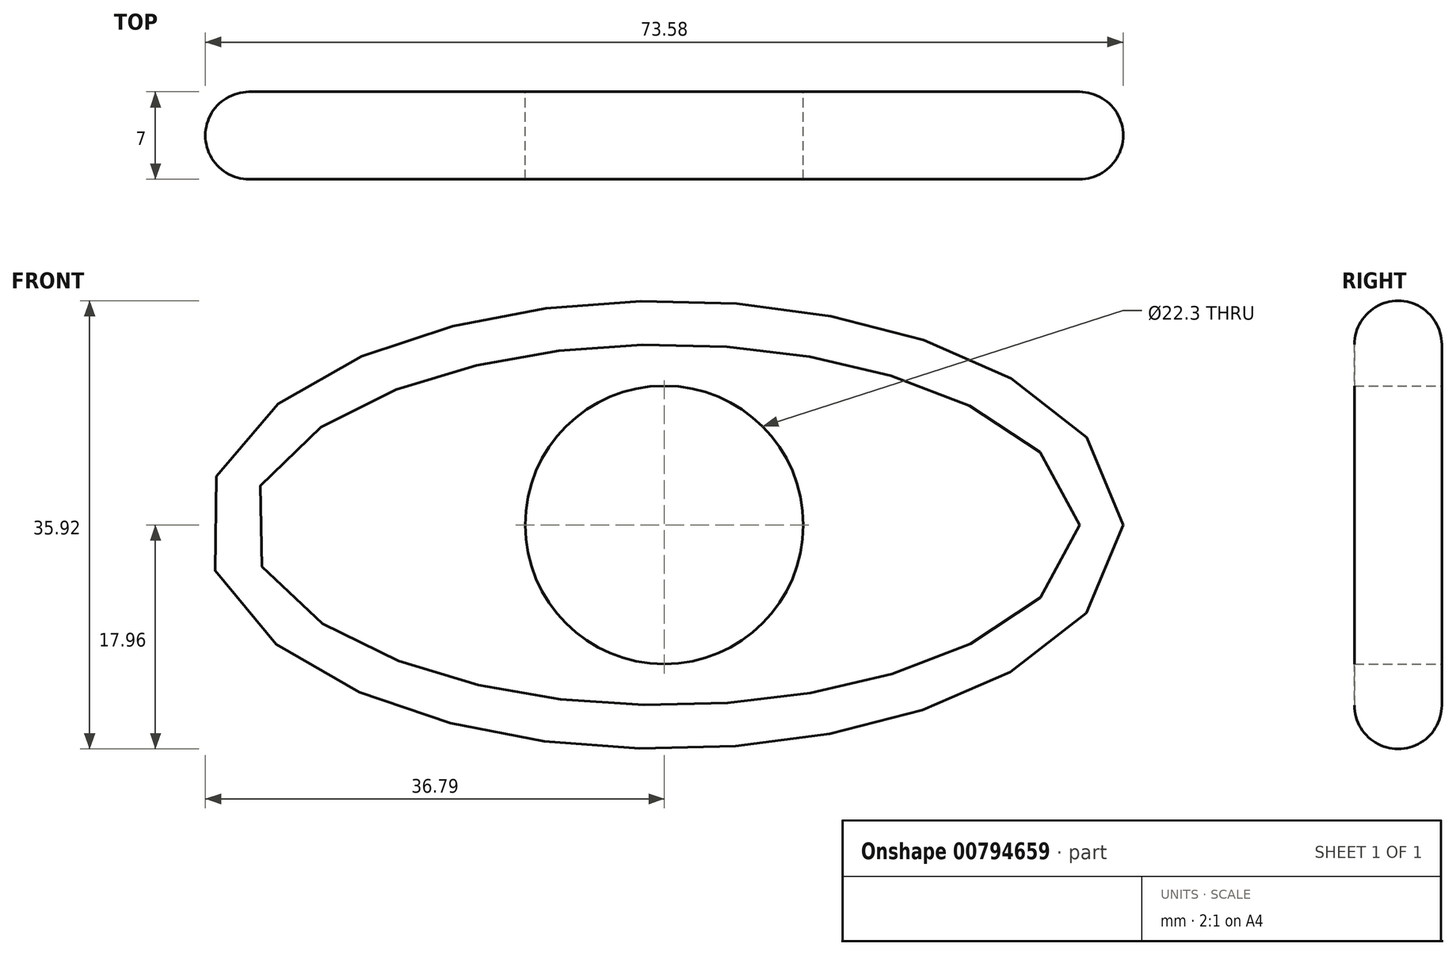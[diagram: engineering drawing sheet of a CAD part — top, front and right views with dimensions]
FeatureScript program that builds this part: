
annotation { "Feature Type Name" : "Feature", "Feature Type Description" : "" }
export const myFeature = defineFeature(function(context is Context, id is Id, definition is map)
    precondition{}
    {
        {
            var Q0;
            Q0=qCreatedBy(makeId("Front.planeOp"),FACE);
            var sketch = newSketch(context, id + "F0", { "sketchPlane" : qUnion([Q0])});
            skCircle(sketch, "E0", {"center": v(0, 0) * mm, "radius": 11.15 * mm});
            skCircle(sketch, "E1", {"center": v(0, 0) * mm, "radius": 15.5 * mm});
            skEllipse(sketch, "E2", {"center": v(0, 0) * mm, "majorRadius": 36.8 * mm, "minorRadius": 17.96 * mm, "majorAxis": v(1, 0)});
            skSolve(sketch);
        }
        {
            var Q0;
            Q0=makeQuery(id+"F0.imprint","IMPRINT",FACE,{"disambiguationData":[TD([[makeQuery(id+"F0.imprint","IMPRINT",EDGE,{"derivedFrom":sQuery(id+"F0.wireOp",EDGE,"E0")}),-1.0]])]});
            var Q1;
            Q1=makeQuery(id+"F0.imprint","IMPRINT",FACE,{"disambiguationData":[TD([[makeQuery(id+"F0.imprint","IMPRINT",EDGE,{"derivedFrom":sQuery(id+"F0.wireOp",EDGE,"E1")}),-1.0]])]});
            extrude(context, id + "F1", {"entities" : qUnion([Q0, Q1]), "depth" : 7 * mm, "offsetDistance" : 25 * mm});
        }
        {
            var Q0;
            Q0=makeQuery(id+"F1.opExtrude","CAP_EDGE",EDGE,{"disambiguationData":[OSD([sQuery(id+"F0.wireOp",EDGE,"E2")])],"isStart":true});
            var Q1;
            Q1=makeQuery(id+"F1.opExtrude","CAP_EDGE",EDGE,{"disambiguationData":[OSD([sQuery(id+"F0.wireOp",EDGE,"E2")])],"isStart":false});
            fillet(context, id + "F2", {"entities" : qUnion([Q0, Q1]), "radius" : 3.5 * mm, "tangentPropagation" : true, "allowEdgeOverflow" : false});
        }
    });
